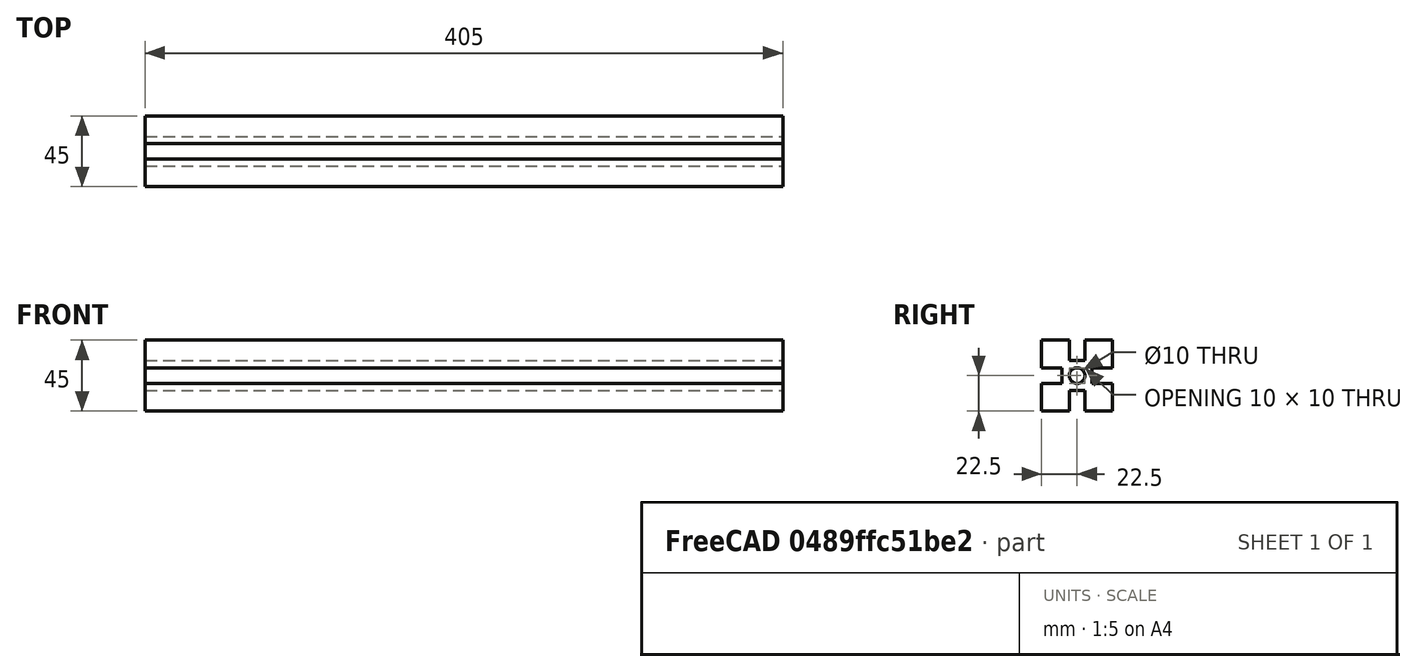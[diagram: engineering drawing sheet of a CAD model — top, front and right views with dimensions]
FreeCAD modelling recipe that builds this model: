
FCSTD DOCUMENT  (FreeCAD 1.0R39109 (Git))
Label: vslot 45x45x405
License: All rights reserved
LicenseURL: https://en.wikipedia.org/wiki/All_rights_reserved
objects: PartDesign::Pocket×3, Part::Feature×1, PartDesign::FeatureBase×1, PartDesign::Pad×1, PartDesign::Body×1
note: 16 computed .brp shape members not serialized (recipe doc carries the construction recipe); baked Part::Feature solids carry a one-line shape summary decoded from their .brp

FEATURE [Part::Feature] Part__Feature  label="1"
  shape: bbox 1000 x 45 x 45 mm, 24 faces (baked)
FEATURE [PartDesign::FeatureBase] BaseFeature
  BaseFeature = -> Part__Feature
  Suppressed = false
FEATURE [PartDesign::Pad] Pad
  BaseFeature = -> BaseFeature
  Direction = (1,0,0)
  Length = 220
  Length2 = 10
  Profile = -> BaseFeature [Face24]
  Refine = true
  Suppressed = false
  Type = 0
FEATURE [PartDesign::Pocket] Pocket
  BaseFeature = -> Pad
  Direction = (-1,0,0)
  Length = 140
  Length2 = 5
  Profile = -> Pad [Face3]
  Refine = true
  Suppressed = false
  Type = 0
FEATURE [PartDesign::Pocket] Pocket001
  BaseFeature = -> Pocket
  Direction = (-1,0,0)
  Length = 480
  Length2 = 5
  Profile = -> Pocket [Face23]
  Refine = true
  Suppressed = false
  Type = 0
FEATURE [PartDesign::Pocket] Pocket002
  BaseFeature = -> Pocket001
  Direction = (-1,0,0)
  Length = 195
  Length2 = 5
  Profile = -> Pocket001 [Face23]
  Refine = true
  Suppressed = false
  Type = 0
FEATURE [PartDesign::Body] Body
  AllowCompound = false
  BaseFeature = -> Part__Feature
  Group = -> [BaseFeature,Pad,Pocket,Pocket001,Pocket002]
  Origin = -> Origin
  Tip = -> Pocket002
